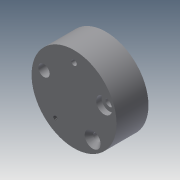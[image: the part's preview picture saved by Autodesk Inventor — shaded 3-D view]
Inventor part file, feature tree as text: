
AUTODESK INVENTOR PART (.ipt)
format: ipt  version: 2015 (Build 190159000, 159)  size: 107,520 bytes
history: native  units: in
note: dims shown in document units (in); Inventor stores cm internally (conversion verified against a paired STEP export)
features: hole x5, sketch x2, extrude x1, projected_geometry x1
ambient origin geometry x8: Origin, YZ Plane, XZ Plane, XY Plane, X Axis, Y Axis, Z Axis, Center Point
bodies: Solid1 (feature_tree)
feature tree (9):
  extrude  "Extrusion1"  Depth=1.5in TaperAngle=0.0deg
  sketch  "Sketch2"  dims[d3=1.9685in d5=360.0deg d7=0.25in d8=0.75in d9=0.375in d10=0.25in d11=0.5635in d12=1.0in d13=0.8108in d14=0.375in d15=0.75in d16=0.75in d17=0.25in d18=0.5635in d19=1.0in d20=0.8108in d21=0.375in d22=0.75in d23=0.75in d24=0.25in d25=0.5635in d26=1.0in d27=0.8108in d28=0.196in d29=0.5in d30=0.75in d31=0.25in d32=0.5635in d33=0.75in d34=0.8108in d35=0.531in d36=0.5in d37=1.125in d38=0.364in d39=0.5635in d40=0.75in d41=0.8108in]
  hole  "Hole1"  [1 undecoded]
  hole  "Hole2"  [1 undecoded]
  hole  "Hole3"  [1 undecoded]
  hole  "Hole4"  [1 undecoded]
  hole  "Hole5"  [1 undecoded]
  sketch  "Sketch1"  dims[d0=4.0in d1=1.5in d2=0.0in]
  projected_geometry  "Projected Loop1"
note: 5 required parameter values undecoded (feature->parameter linkage not recoverable at this tier; creation-order binding heuristic only, values carry confidence <= 0.55)
